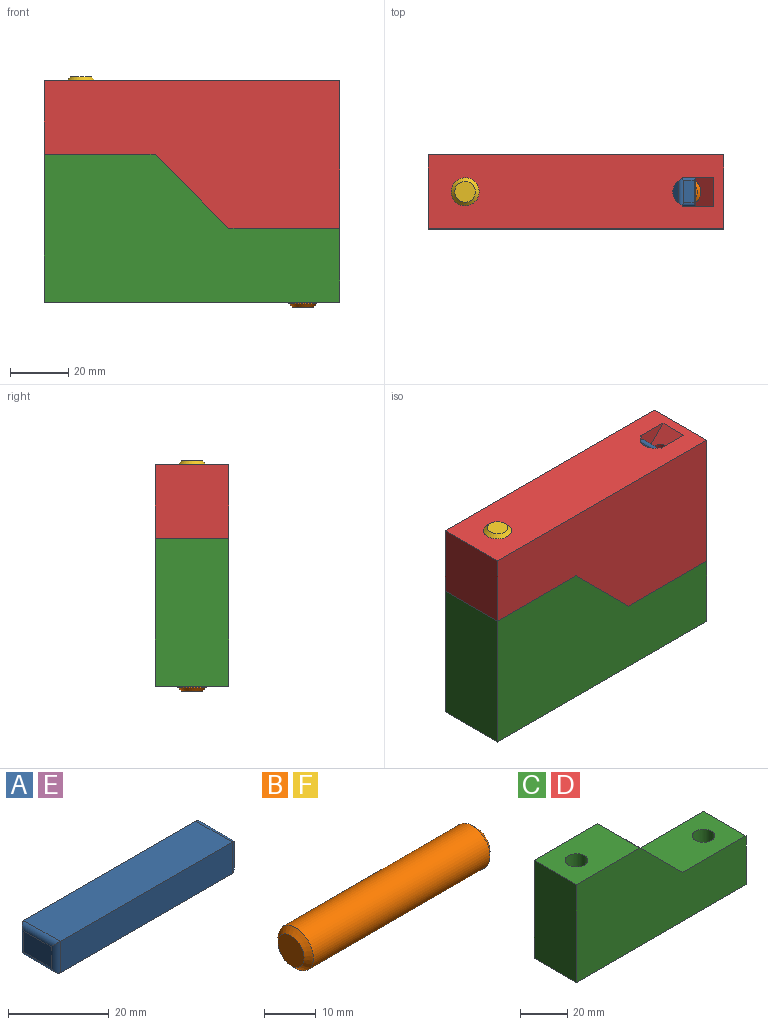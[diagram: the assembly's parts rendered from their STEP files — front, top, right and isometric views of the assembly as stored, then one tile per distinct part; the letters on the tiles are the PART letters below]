
ASSEMBLY  parts=6 mates=5
PART A: 14 faces, bbox 50.8x10.2x7.6 mm
  f0: plane 7.62x5.08mm, normal (-1,0,0), area 38.7mm2, adj f6,f7,f8,f9
  f1: plane 48.26x10.16mm, normal (0,0,-1), area 490.3mm2, adj f4,f5,f9,f13
  f2: plane 7.62x5.08mm, normal (1,0,0), area 38.7mm2, adj f10,f11,f12,f13
  f3: plane 48.26x10.16mm, normal (0,0,1), area 490.3mm2, adj f4,f5,f6,f10
  f4: plane 48.26x7.62mm, normal (0,-1,0), area 367.7mm2, adj f1,f3,f7,f11
  f5: plane 48.26x7.62mm, normal (0,1,0), area 367.7mm2, adj f1,f3,f8,f12
  f6: cylinder r=1.27mm len=10.16mm, axis (0,-1,0), area 18.4mm2, adj f0,f3,f7,f8
  f7: cylinder r=1.27mm len=7.62mm, axis (0,0,1), area 13.4mm2, adj f0,f4,f6,f9
  f8: cylinder r=1.27mm len=7.62mm, axis (0,0,-1), area 13.4mm2, adj f0,f5,f6,f9
  f9: cylinder r=1.27mm len=10.16mm, axis (0,1,0), area 18.4mm2, adj f0,f1,f7,f8
  f10: cylinder r=1.27mm len=10.16mm, axis (0,1,0), area 18.4mm2, adj f2,f3,f11,f12
  f11: cylinder r=1.27mm len=7.62mm, axis (0,0,-1), area 13.4mm2, adj f2,f4,f10,f13
  f12: cylinder r=1.27mm len=7.62mm, axis (0,0,1), area 13.4mm2, adj f2,f5,f10,f13
  f13: cylinder r=1.27mm len=10.16mm, axis (0,-1,0), area 18.4mm2, adj f1,f2,f11,f12
PART B: 5 faces, bbox 50.8x9.7x9.7 mm
  f0: plane 7.11x7.11mm, normal (1,0,0), area 39.7mm2, adj f3
  f1: plane 7.11x7.11mm, normal (-1,0,0), area 39.7mm2, adj f4
  f2: cylinder r=4.83mm len=48.26mm, axis (-1,0,0), area 1463.4mm2, adj f3,f4
  f3: cone r=4.83mm half-angle=45deg, axis (-1,0,0), area 47.3mm2, adj f0,f2
  f4: cone r=3.56mm half-angle=45deg, axis (1,0,0), area 47.3mm2, adj f1,f2
PART C: 15 faces, bbox 101.6x25.4x50.8 mm
  f0: plane 101.6x25.4mm, normal (0,0,-1), area 2376mm2, adj f1,f4,f5,f7,f8,f10,f11,f12
  f1: cylinder r=4.83mm len=9.15mm, axis (0,0,1), area 25.6mm2, adj f0,f14
  f2: plane 25.4x25.4mm, normal (0.71,0,0.71), area 835mm2, adj f3,f6,f7,f8,f11,f12,f13,f14
  f3: plane 38.1x25.4mm, normal (0,0,1), area 894.6mm2, adj f2,f4,f7,f8,f9
  f4: plane 50.8x25.4mm, normal (-1,0,0), area 1290.3mm2, adj f0,f3,f7,f8
  f5: plane 25.4x25.4mm, normal (1,0,0), area 645.2mm2, adj f0,f6,f7,f8
  f6: plane 38.1x25.4mm, normal (0,0,1), area 894.6mm2, adj f2,f5,f7,f8,f10
  f7: plane 101.6x50.8mm, normal (0,-1,0), area 3871mm2, adj f0,f2,f3,f4,f5,f6
  f8: plane 101.6x50.8mm, normal (0,1,0), area 3871mm2, adj f0,f2,f3,f4,f5,f6
  f9: cylinder r=4.83mm len=46.46mm, axis (0,0,1), area 1260.3mm2, adj f3,f13
  f10: cylinder r=4.83mm len=25.4mm, axis (0,0,1), area 770.2mm2, adj f0,f6
  f11: plane 48.11x42.72mm, normal (0,1,0), area 431.3mm2, adj f0,f2,f13,f14
  f12: plane 48.11x42.72mm, normal (0,-1,0), area 431.3mm2, adj f0,f2,f13,f14
  f13: plane 42.72x42.72mm, normal (0.71,0,-0.71), area 510.3mm2, adj f0,f2,f9,f11,f12
  f14: plane 37.33x37.33mm, normal (-0.71,0,0.71), area 505.3mm2, adj f0,f1,f2,f11,f12
PART D: same geometry as C
PART E: same geometry as A
PART F: same geometry as B
PLACE A rot(axis=(0,-1,0),45deg) t=(22.89,39.36,87.06)mm
PLACE B rot(axis=(0,-1,0),90deg) t=(24.34,34.28,65.81)mm
PLACE C t=(32.21,46.98,16.71)mm
PLACE D rot(axis=(0,-1,0),180deg) t=(-69.39,46.98,92.91)mm
PLACE E rot(axis=(-0.92,0,-0.38),180deg) t=(-24.14,29.2,58.49)mm
PLACE F rot(axis=(0,-1,0),90deg) t=(-51.86,34.28,94.18)mm
MATE planar C.f1 <-> D.f10  axis (0,0,1) through (-56.69,34.28,67.51)mm
MATE planar E.f1 <-> C.f13  axis (-0.71,0,0.71) through (-42.1,34.28,40.53)mm
MATE planar A.f1 <-> D.f13  axis (0.71,0,-0.71) through (4.93,34.28,69.1)mm
MATE cylindrical F.f2 <-> D.f10  axis (0,0,-1) through (-56.69,34.28,92.91)mm
MATE cylindrical B.f2 <-> D.f1  axis (0,0,-1) through (19.51,34.28,64.54)mm
